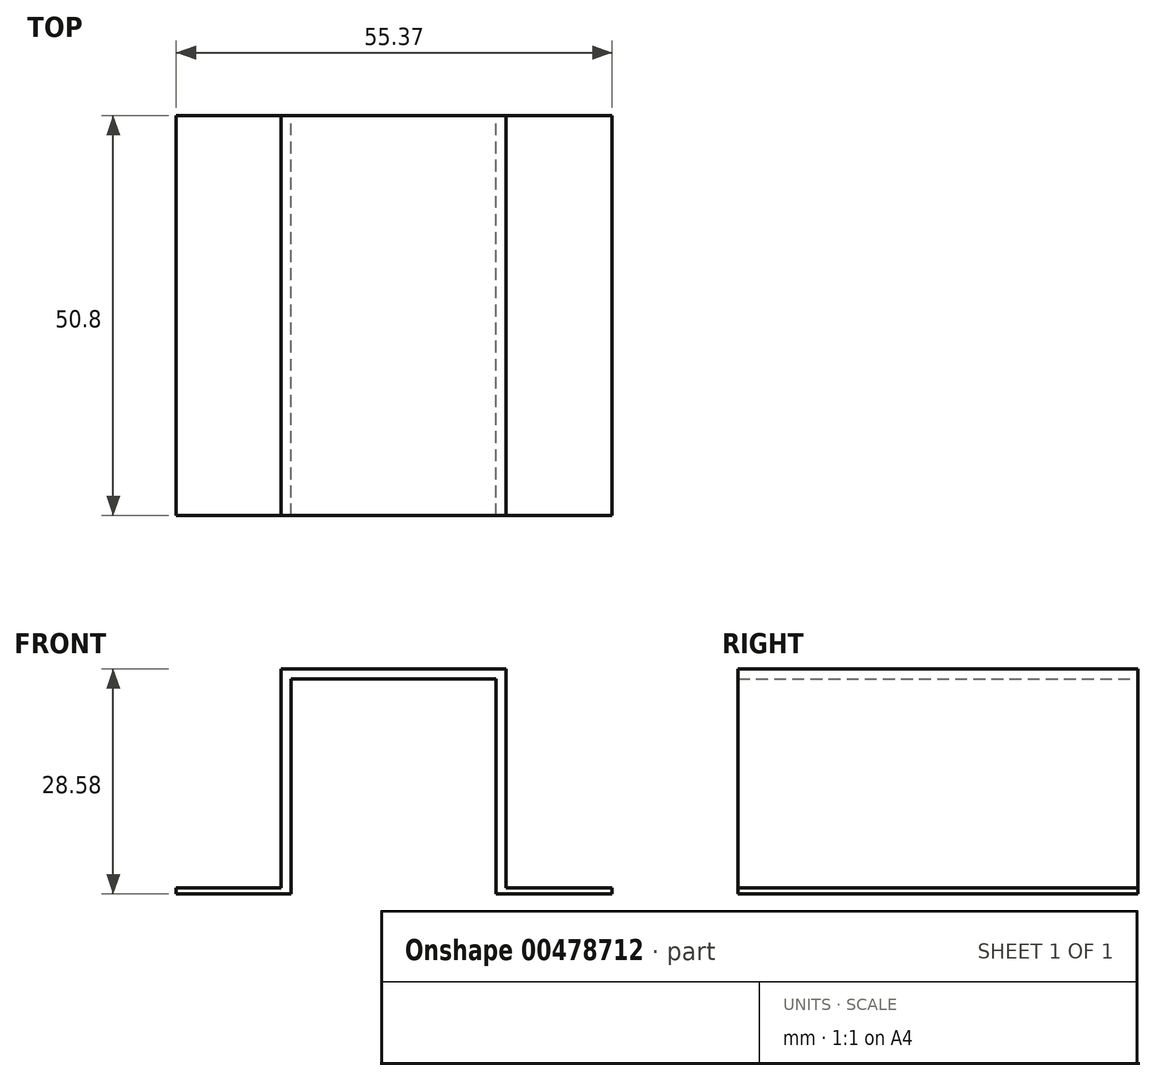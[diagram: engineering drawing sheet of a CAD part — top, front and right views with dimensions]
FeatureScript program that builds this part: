
annotation { "Feature Type Name" : "Feature", "Feature Type Description" : "" }
export const myFeature = defineFeature(function(context is Context, id is Id, definition is map)
    precondition{}
    {
        {
            var Q0;
            Q0=qCreatedBy(makeId("Front.planeOp"),FACE);
            var sketch = newSketch(context, id + "F0", { "sketchPlane" : qUnion([Q0])});
            skLineSegment(sketch, "E0.bottom", {"start": v(-34.15, -1.42) * mm, "end": v(-62.73, -1.42) * mm});
            skLineSegment(sketch, "E0.top", {"start": v(-34.15, -30) * mm, "end": v(-62.73, -30) * mm});
            skLineSegment(sketch, "E0.left", {"start": v(-34.15, -1.42) * mm, "end": v(-34.15, -30) * mm});
            skLineSegment(sketch, "E0.right", {"start": v(-62.73, -1.42) * mm, "end": v(-62.73, -30) * mm});
            skSolve(sketch);
        }
        {
            var Q0;
            Q0=makeQuery(id+"F0.imprint","IMPRINT",FACE,{"disambiguationData":[TD([[makeQuery(id+"F0.imprint","IMPRINT",EDGE,{"derivedFrom":sQuery(id+"F0.wireOp",EDGE,"E0.bottom")}),1.0]])]});
            extrude(context, id + "F1", {"entities" : qUnion([Q0]), "depth" : 50.8 * mm});
        }
        {
            var Q0;
            Q0=makeQuery(id+"F1.opExtrude","CAP_FACE",FACE,{"disambiguationData":[OSD([sQuery(id+"F0.wireOp",EDGE,"E0.bottom"),sQuery(id+"F0.wireOp",EDGE,"E0.top"),sQuery(id+"F0.wireOp",EDGE,"E0.left"),sQuery(id+"F0.wireOp",EDGE,"E0.right")])],"isStart":false});
            var Q1;
            Q1=makeQuery(id+"F1.opExtrude","CAP_FACE",FACE,{"disambiguationData":[OSD([sQuery(id+"F0.wireOp",EDGE,"E0.bottom"),sQuery(id+"F0.wireOp",EDGE,"E0.top"),sQuery(id+"F0.wireOp",EDGE,"E0.left"),sQuery(id+"F0.wireOp",EDGE,"E0.right")])],"isStart":true});
            var Q2;
            Q2=makeQuery(id+"F1.opExtrude","SWEPT_FACE",FACE,{"disambiguationData":[OSD([sQuery(id+"F0.wireOp",EDGE,"E0.top")])]});
            shell(context, id + "F2", {"entities" : qUnion([Q0, Q1, Q2]), "thickness" : 1.27 * mm});
        }
        {
            var Q0;
            Q0=makeQuery(id+"F1.opExtrude","SWEPT_FACE",FACE,{"disambiguationData":[OSD([sQuery(id+"F0.wireOp",EDGE,"E0.top")])]});
            var sketch = newSketch(context, id + "F3", { "sketchPlane" : qUnion([Q0])});
            skLineSegment(sketch, "E1", {"start": v(-62.73, 50.8) * mm, "end": v(-76.03, 50.8) * mm});
            skLineSegment(sketch, "E2", {"start": v(-76.03, 50.8) * mm, "end": v(-76.03, 0) * mm});
            skLineSegment(sketch, "E3", {"start": v(-76.03, 0) * mm, "end": v(-62.73, 0) * mm});
            skSolve(sketch);
        }
        {
            var Q0;
            Q0=makeQuery(id+"F2.opShell","OFFSET_FACE",FACE,{"disambiguationData":[OSD([sQuery(id+"F0.wireOp",EDGE,"E0.top")])]});
            var sketch = newSketch(context, id + "F4", { "sketchPlane" : qUnion([Q0])});
            skLineSegment(sketch, "E4", {"start": v(-34.15, 50.8) * mm, "end": v(-20.66, 50.8) * mm});
            skLineSegment(sketch, "E5", {"start": v(-20.66, 50.8) * mm, "end": v(-20.66, 0) * mm});
            skLineSegment(sketch, "E6", {"start": v(-20.66, 0) * mm, "end": v(-34.15, 0) * mm});
            skSolve(sketch);
        }
        {
            var Q0;
            Q0=makeQuery(id+"F3.imprint","IMPRINT",FACE,{"disambiguationData":[TD([[makeQuery(id+"F3.imprint","IMPRINT",EDGE,{"derivedFrom":sQuery(id+"F3.wireOp",EDGE,"E1")}),1.0]])]});
            extrude(context, id + "F5", {"entities" : qUnion([Q0]), "operationType" : NewBodyOperationType.ADD, "oppositeDirection" : true, "depth" : 0.76 * mm});
        }
        {
            var Q0;
            Q0=makeQuery(id+"F4.imprint","IMPRINT",FACE,{"disambiguationData":[TD([[makeQuery(id+"F4.imprint","IMPRINT",EDGE,{"derivedFrom":sQuery(id+"F4.wireOp",EDGE,"E4")}),-1.0]])]});
            extrude(context, id + "F6", {"entities" : qUnion([Q0]), "operationType" : NewBodyOperationType.ADD, "oppositeDirection" : true, "depth" : 0.76 * mm});
        }
    });
